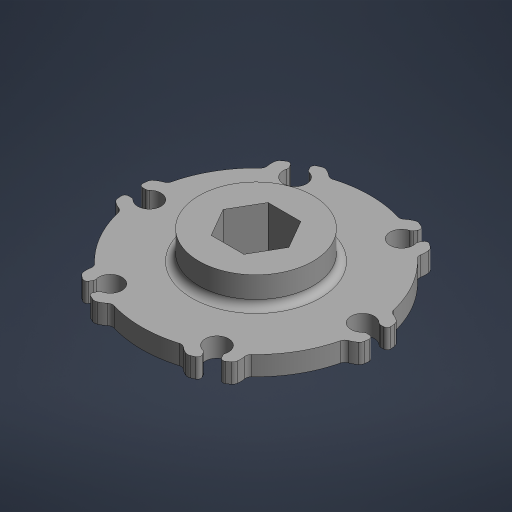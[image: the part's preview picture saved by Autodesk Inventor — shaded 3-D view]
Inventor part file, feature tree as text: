
AUTODESK INVENTOR PART (.ipt)
format: ipt  version: 2023.4 (Build 274418000, 418)  size: 285,696 bytes
history: native  units: mm (DEFAULTED — no unit token found)
features: extrude x2, fillet x2, delete_face x2, sketch x2, chamfer x1
ambient origin geometry x8: Origin, YZ Plane, XZ Plane, XY Plane, X Axis, Y Axis, Z Axis, Center Point
bodies: Solid1 (feature_tree)
feature tree (9):
  extrude  "Extrusion2"  TaperAngle=0.0deg  [1 undecoded]
  fillet  "Fillet1"  Radius=12.7mm
  chamfer  "Chamfer1"  Distance=6.35mm
  delete_face  "Delete Face1"
  delete_face  "Delete Face2"
  extrude  "Extrusion1"  Depth=4.318mm TaperAngle=0.0deg
  sketch  "Sketch1"  dims[d0=24.384mm d1=0.0mm d2=0.0mm d3=12.7mm]
  sketch  "Sketch2"  dims[d4=25.4mm d5=6.35mm d6=0.0mm d7=4.318mm d8=0.0mm d9=1.5875mm d10=0.635mm d11=3.175mm d12=45.0deg]
  fillet  "Fillet7"  Radius=1.5875mm
note: 1 required parameter value undecoded (feature->parameter linkage not recoverable at this tier; creation-order binding heuristic only, values carry confidence <= 0.55)
